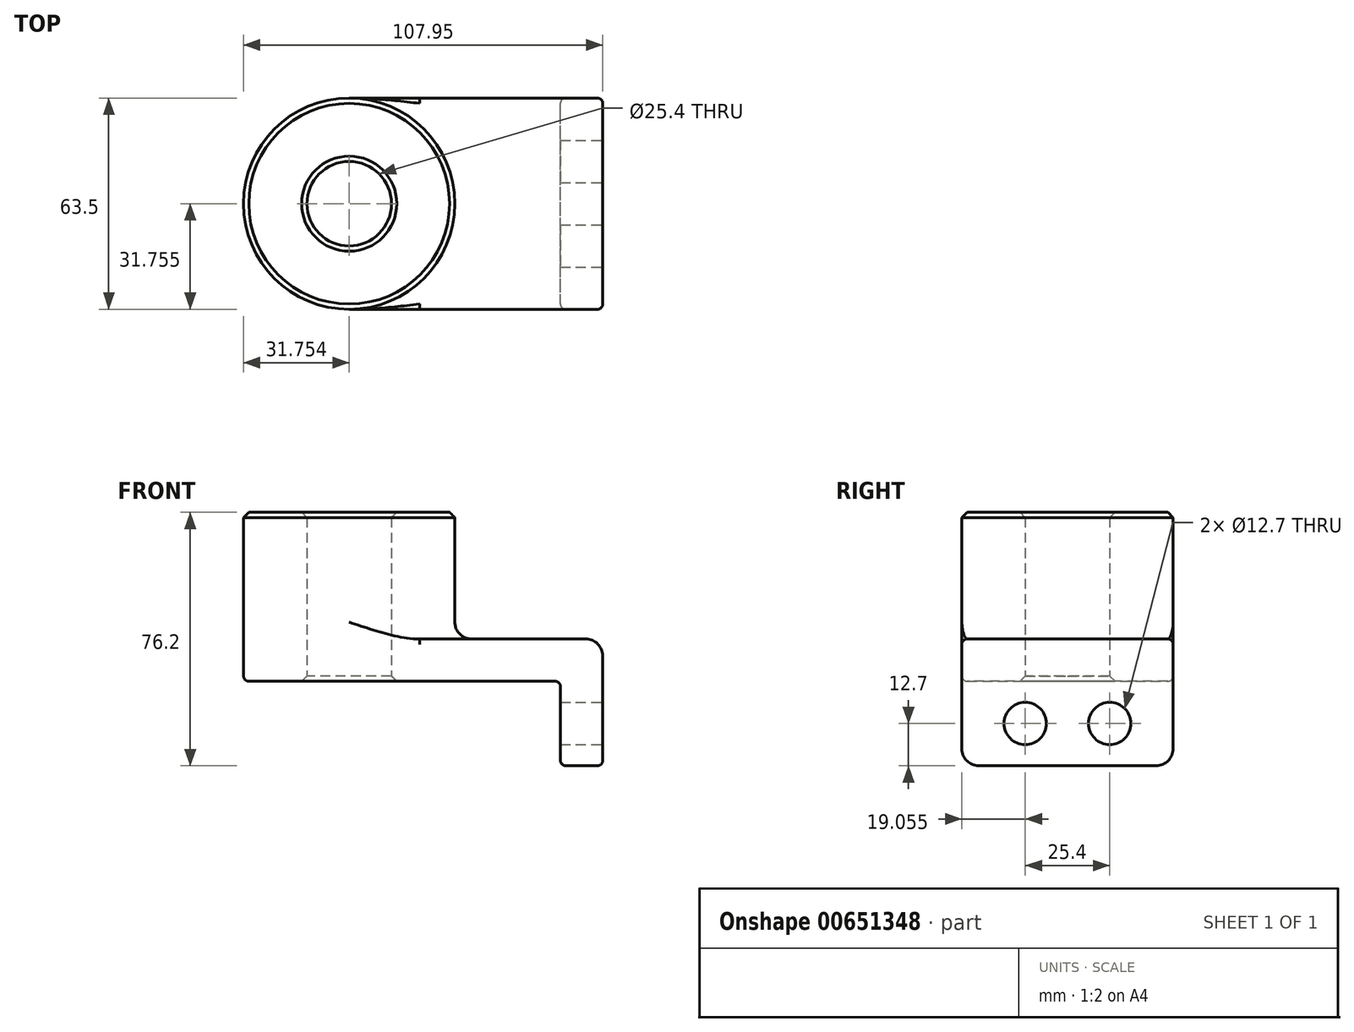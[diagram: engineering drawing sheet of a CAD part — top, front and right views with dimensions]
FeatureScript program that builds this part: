
annotation { "Feature Type Name" : "Feature", "Feature Type Description" : "" }
export const myFeature = defineFeature(function(context is Context, id is Id, definition is map)
    precondition{}
    {
        {
            var Q0;
            Q0=qCreatedBy(makeId("Top.planeOp"),FACE);
            var sketch = newSketch(context, id + "F0", { "sketchPlane" : qUnion([Q0])});
            skLineSegment(sketch, "E0.bottom", {"start": v(10.1, -29.28) * mm, "end": v(-66.1, -29.28) * mm});
            skLineSegment(sketch, "E0.top", {"start": v(10.1, 34.22) * mm, "end": v(-66.1, 34.22) * mm});
            skLineSegment(sketch, "E0.left", {"start": v(10.1, -29.28) * mm, "end": v(10.1, 34.22) * mm});
            skLineSegment(sketch, "E0.right", {"start": v(-66.1, -29.28) * mm, "end": v(-66.1, 34.22) * mm});
            skPoint(sketch, "E0.middle", {"position": v(-28, 2.47) * mm});
            skCircle(sketch, "E1", {"center": v(-66.1, 2.47) * mm, "radius": 31.75 * mm});
            skCircle(sketch, "E2", {"center": v(-66.1, 2.47) * mm, "radius": 12.7 * mm});
            skSolve(sketch);
        }
        {
            var Q0;
            Q0=qSketchRegion(id+"F0",true);
            extrude(context, id + "F1", {"entities" : qUnion([Q0]), "depth" : 12.7 * mm});
        }
        {
            var Q0;
            {var subQ1=sQuery(id+"F0.wireOp",EDGE,"E0.right");var subQ3=sQuery(id+"F0.wireOp",EDGE,"E2");var subQ4=makeQuery(id+"F0.imprint","INTERSECT",VERTEX,{"disambiguationData":[OD(0.0)],"derivedFrom":[subQ1,subQ3]});Q0=makeQuery(id+"F0.imprint","IMPRINT",FACE,{"disambiguationData":[TD([[makeQuery(id+"F0.imprint","IMPRINT",EDGE,{"disambiguationData":[TD([[subQ4,1.0]])],"derivedFrom":subQ3}),-1.0]])]});}
            var Q1;
            {var subQ1=sQuery(id+"F0.wireOp",EDGE,"E0.right");var subQ3=sQuery(id+"F0.wireOp",EDGE,"E2");var subQ4=makeQuery(id+"F0.imprint","INTERSECT",VERTEX,{"disambiguationData":[OD(0.0)],"derivedFrom":[subQ1,subQ3]});Q1=makeQuery(id+"F0.imprint","IMPRINT",FACE,{"disambiguationData":[TD([[makeQuery(id+"F0.imprint","IMPRINT",EDGE,{"disambiguationData":[TD([[subQ4,-1.0]])],"derivedFrom":subQ3}),-1.0]])]});}
            extrude(context, id + "F2", {"entities" : qUnion([Q0, Q1]), "operationType" : NewBodyOperationType.ADD, "depth" : 50.8 * mm});
        }
        {
            var Q0;
            Q0=makeQuery(id+"F1.opExtrude","SWEPT_FACE",FACE,{"disambiguationData":[OSD([sQuery(id+"F0.wireOp",EDGE,"E0.left")])]});
            var sketch = newSketch(context, id + "F3", { "sketchPlane" : qUnion([Q0])});
            skLineSegment(sketch, "E3.bottom", {"start": v(-29.28, 12.7) * mm, "end": v(34.22, 12.7) * mm});
            skLineSegment(sketch, "E3.top", {"start": v(-29.28, -25.4) * mm, "end": v(34.22, -25.4) * mm});
            skLineSegment(sketch, "E3.left", {"start": v(-29.28, 12.7) * mm, "end": v(-29.28, -25.4) * mm});
            skLineSegment(sketch, "E3.right", {"start": v(34.22, 12.7) * mm, "end": v(34.22, -25.4) * mm});
            skCircle(sketch, "E4", {"center": v(-10.23, -12.7) * mm, "radius": 6.35 * mm});
            skLineSegment(sketch, "E5", {"start": v(2.47, 0) * mm, "end": v(2.47, -25.4) * mm, "construction": true});
            skCircle(sketch, "E6.MirrorC", {"center": v(15.17, -12.7) * mm, "radius": 6.35 * mm});
            skSolve(sketch);
        }
        {
            var Q0;
            Q0=qSketchRegion(id+"F3",true);
            extrude(context, id + "F4", {"entities" : qUnion([Q0]), "operationType" : NewBodyOperationType.ADD, "oppositeDirection" : true, "depth" : 12.7 * mm});
        }
        {
            var Q0;
            {var subQ0=sQuery(id+"F0.wireOp",EDGE,"E1");Q0=makeQuery(id+"F2.boolean.opBoolean","INTERSECT",EDGE,{"derivedFrom":[makeQuery(id+"F1.opExtrude","CAP_FACE",FACE,{"disambiguationData":[OSD([sQuery(id+"F0.wireOp",EDGE,"E0.bottom"),sQuery(id+"F0.wireOp",EDGE,"E0.top"),sQuery(id+"F0.wireOp",EDGE,"E0.left"),subQ0,sQuery(id+"F0.wireOp",EDGE,"E2")])],"isStart":false}),makeQuery(id+"F2.opExtrude","SWEPT_FACE",FACE,{"disambiguationData":[OSD([subQ0])]})]});}
            var Q1;
            Q1=makeQuery(id+"F1.opExtrude","CAP_EDGE",EDGE,{"disambiguationData":[OSD([sQuery(id+"F0.wireOp",EDGE,"E0.left")])],"isStart":false});
            var Q2;
            Q2=makeQuery(id+"F4.opExtrude","SWEPT_EDGE",EDGE,{"disambiguationData":[OSD([sQuery(id+"F3.wireOp",EDGE,"E3.top"),sQuery(id+"F3.wireOp",EDGE,"E3.left")])]});
            var Q3;
            Q3=makeQuery(id+"F4.opExtrude","SWEPT_EDGE",EDGE,{"disambiguationData":[OSD([sQuery(id+"F3.wireOp",EDGE,"E3.top"),sQuery(id+"F3.wireOp",EDGE,"E3.right")])]});
            fillet(context, id + "F5", {"entities" : qUnion([Q0, Q1, Q2, Q3]), "radius" : 5.08 * mm, "tangentPropagation" : true, "allowEdgeOverflow" : false});
        }
        {
            var Q0;
            {var subQ0=sQuery(id+"F0.wireOp",EDGE,"E0.top");var subQ1=sQuery(id+"F0.wireOp",EDGE,"E1");Q0=makeQuery(id+"F5.opFillet","BLEND_EDGE",EDGE,{"blendedFrom":[makeQuery(id+"F2.boolean.opBoolean","INTERSECT",EDGE,{"derivedFrom":[makeQuery(id+"F1.opExtrude","CAP_FACE",FACE,{"disambiguationData":[OSD([sQuery(id+"F0.wireOp",EDGE,"E0.bottom"),subQ0,sQuery(id+"F0.wireOp",EDGE,"E0.left"),subQ1,sQuery(id+"F0.wireOp",EDGE,"E2")])],"isStart":false}),makeQuery(id+"F2.opExtrude","SWEPT_FACE",FACE,{"disambiguationData":[OSD([subQ1])]})]}),makeQuery(id+"F4.boolean.opBoolean","MERGE",FACE,{"derivedFrom":[makeQuery(id+"F1.opExtrude","SWEPT_FACE",FACE,{"disambiguationData":[OSD([subQ0])]}),makeQuery(id+"F4.opExtrude","SWEPT_FACE",FACE,{"disambiguationData":[OSD([sQuery(id+"F3.wireOp",EDGE,"E3.right")])]})]})],"blendedInto":[makeQuery(id+"F4.boolean.opBoolean","MERGE",FACE,{"derivedFrom":[makeQuery(id+"F1.opExtrude","SWEPT_FACE",FACE,{"disambiguationData":[OSD([subQ0])]}),makeQuery(id+"F4.opExtrude","SWEPT_FACE",FACE,{"disambiguationData":[OSD([sQuery(id+"F3.wireOp",EDGE,"E3.right")])]})]})]});}
            var Q1;
            Q1=makeQuery(id+"F1.opExtrude","CAP_EDGE",EDGE,{"disambiguationData":[OSD([sQuery(id+"F0.wireOp",EDGE,"E0.top")])],"isStart":false});
            var Q2;
            Q2=makeQuery(id+"F1.opExtrude","CAP_EDGE",EDGE,{"disambiguationData":[OSD([sQuery(id+"F0.wireOp",EDGE,"E0.bottom")])],"isStart":true});
            var Q3;
            Q3=makeQuery(id+"F4.opExtrude","CAP_EDGE",EDGE,{"disambiguationData":[OSD([sQuery(id+"F3.wireOp",EDGE,"E3.left")])],"isStart":false});
            var Q4;
            Q4=makeQuery(id+"F4.boolean.opBoolean","INTERSECT",EDGE,{"derivedFrom":[makeQuery(id+"F1.opExtrude","CAP_FACE",FACE,{"disambiguationData":[OSD([sQuery(id+"F0.wireOp",EDGE,"E0.bottom"),sQuery(id+"F0.wireOp",EDGE,"E0.top"),sQuery(id+"F0.wireOp",EDGE,"E0.left"),sQuery(id+"F0.wireOp",EDGE,"E1"),sQuery(id+"F0.wireOp",EDGE,"E2")])],"isStart":true}),makeQuery(id+"F4.opExtrude","CAP_FACE",FACE,{"disambiguationData":[OSD([sQuery(id+"F3.wireOp",EDGE,"E3.bottom"),sQuery(id+"F3.wireOp",EDGE,"E3.top"),sQuery(id+"F3.wireOp",EDGE,"E3.left"),sQuery(id+"F3.wireOp",EDGE,"E3.right"),sQuery(id+"F3.wireOp",EDGE,"E4"),sQuery(id+"F3.wireOp",EDGE,"E6.MirrorC")])],"isStart":false})]});
            fillet(context, id + "F6", {"entities" : qUnion([Q0, Q1, Q2, Q3, Q4]), "radius" : 1.59 * mm, "tangentPropagation" : true, "allowEdgeOverflow" : false});
        }
        {
            var Q0;
            {var subQ0=sQuery(id+"F0.wireOp",EDGE,"E2");Q0=makeQuery(id+"F2.boolean.opBoolean","MERGE",FACE,{"derivedFrom":[makeQuery(id+"F1.opExtrude","SWEPT_FACE",FACE,{"disambiguationData":[OSD([subQ0])]}),makeQuery(id+"F2.opExtrude","SWEPT_FACE",FACE,{"disambiguationData":[OSD([subQ0])]})]});}
            var Q1;
            Q1=makeQuery(id+"F2.opExtrude","CAP_EDGE",EDGE,{"disambiguationData":[OSD([sQuery(id+"F0.wireOp",EDGE,"E1")])],"isStart":false});
            chamfer(context, id + "F7", {"entities" : qUnion([Q0, Q1]), "width" : 1.59 * mm, "tangentPropagation" : true});
        }
    });
